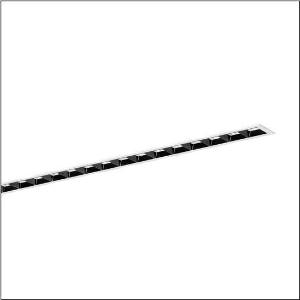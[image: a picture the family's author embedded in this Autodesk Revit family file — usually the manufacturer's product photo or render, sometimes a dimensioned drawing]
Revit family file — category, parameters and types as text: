
# Revit family: silica_r__21_51mx11db35wb_5c76
name_source: partatom
category: Lighting Fixtures
units: mm (PartAtom-declared; Revit-internal decimal feet)

## family parameters
Cut with Voids When Loaded = No
Host = Face
Light Source = No
Part Type = Normal
Room Calculation Point = No
Round Connector Dimension = Use Diameter
Shared = No

## types (1)
- --- (1 x LED, 5400 lm, 34.3 W, 3000K)
    Apparent Load = 34 VA
    CIE Flux Codes = 87 99 100 100 100
    Color Rendering = 80
    Color Temperature = 3000K
    Default Elevation = 1800 mm
    Description = Silica® 21, office luminaire, primary light control with darklight reflector, of PMMA, black, CAT 2 (L<= 3000cd/m²), light emission: direct distribution, primary light characteristic: symmetric, installation type: recessed, LED, rated luminous flux: 5.400lm, luminous efficacy: 157lm/W, light colour: 830, colour temperature: 3000K, with terminal, 3+2-pole, max. 2.5mm², mains connection: 220..240V, AC, 50/60Hz, rated input power: 34.3W, luminaire housing, of aluminium, traffic white (RAL 9016), length: 1.528mm, width: 79mm, height: 53mm, protection rating (complete): IP20, insulation class (complete): insulation class I (protective earthing), certification: CE, permissible operating ambient temperature: 0..+35°C, standard: EN 50419, packaging unit: 1 piece
    Height = 0 mm  [stored 0 ft]
    Lamp = 1 x LED
    Lamp Light Flux = 5400 lm
    Lamp Power = 34.3 W
    Lamp count = 1
    Length = 1527 mm
    Luminous efficacy = 157 lm/W
    Manufacturer = Siteco
    ModVariant = No
    Model = 51MX11DB35WB
    Mounting Place = Ceiling
    Mounting Type = Recessed
    Number of Poles = 1
    OnlyDefault = Yes
    Power Factor = 1
    Product Name = Silica® 21
    Product group = office luminaire | ceiling recessed
    ProductGroupID = 401
    Protection Class = Protection class I
    Protection Degree = IP 20
    RLX_Detail_Level = 1
    RLX_Emergency_Light_Flux = 0 lm
    RLX_Emergency_Type = 0
    RLX_Emergency_Type_DB = No
    RlxData = <blob elided: 42377 chars, md5=22c8ffc3>
    Socket = socket
    Standby Power = 0 W
    System Light Flux = 5400 lm
    System Power = 34 W
    Type Comments = factory setting: luminous flux: 100 % | dim-lin: 254 | 393 mA
    Type Image = l_1297791.jpg
    URL = http://relux.com
    VarID = @adj_054107
    Voltage = 0 V
    Weight = 0.00 kg
    Width = 79 mm

note: [stored X ft] marks values corroborated as IEEE doubles in the binary element streams (Revit-internal decimal feet)

## geometry (parser evidence)
native form markers: Blend x4, Sweep x9
no freeform markers — native parametric forms only
